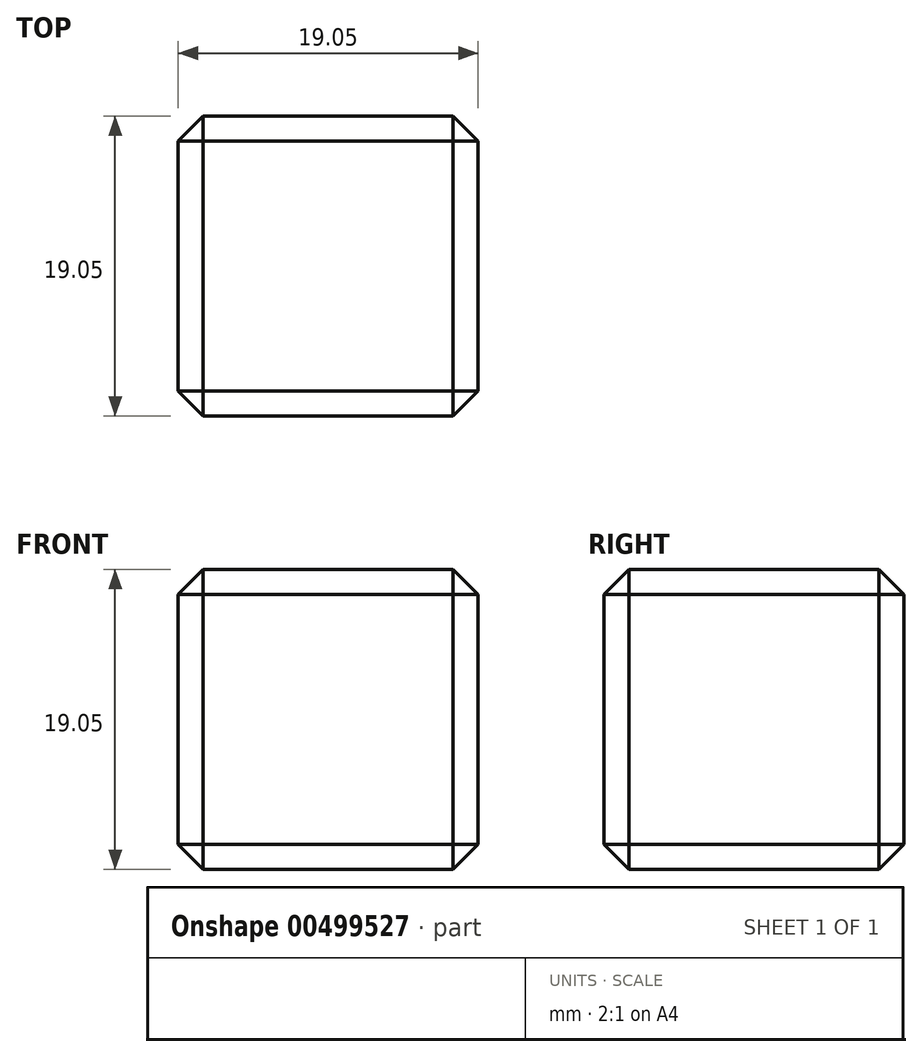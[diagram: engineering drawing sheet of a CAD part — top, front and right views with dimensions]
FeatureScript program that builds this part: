
annotation { "Feature Type Name" : "Feature", "Feature Type Description" : "" }
export const myFeature = defineFeature(function(context is Context, id is Id, definition is map)
    precondition{}
    {
        {
            var Q0;
            Q0=qCreatedBy(makeId("Top.planeOp"),FACE);
            var sketch = newSketch(context, id + "F0", { "sketchPlane" : qUnion([Q0])});
            skLineSegment(sketch, "E0.bottom", {"start": v(0, 0) * mm, "end": v(19.05, 0) * mm});
            skLineSegment(sketch, "E0.top", {"start": v(0, -19.05) * mm, "end": v(19.05, -19.05) * mm});
            skLineSegment(sketch, "E0.left", {"start": v(0, 0) * mm, "end": v(0, -19.05) * mm});
            skLineSegment(sketch, "E0.right", {"start": v(19.05, 0) * mm, "end": v(19.05, -19.05) * mm});
            skSolve(sketch);
        }
        {
            var Q0;
            Q0 = qSketchRegion(id + "F0", true);
            extrude(context, id + "F1", {"entities" : qUnion([Q0]), "depth" : 19.05 * mm});
        }
        {
            var Q0;
            Q0=makeQuery(id+"F1.opExtrude","SWEPT_EDGE",EDGE,{"disambiguationData":[OSD([sQuery(id+"F0.wireOp",EDGE,"E0.top"),sQuery(id+"F0.wireOp",EDGE,"E0.right")])]});
            var Q1;
            Q1=makeQuery(id+"F1.opExtrude","CAP_EDGE",EDGE,{"disambiguationData":[OSD([sQuery(id+"F0.wireOp",EDGE,"E0.top")])],"isStart":true});
            var Q2;
            Q2=makeQuery(id+"F1.opExtrude","CAP_EDGE",EDGE,{"disambiguationData":[OSD([sQuery(id+"F0.wireOp",EDGE,"E0.right")])],"isStart":true});
            var Q3;
            Q3=makeQuery(id+"F1.opExtrude","SWEPT_EDGE",EDGE,{"disambiguationData":[OSD([sQuery(id+"F0.wireOp",EDGE,"E0.bottom"),sQuery(id+"F0.wireOp",EDGE,"E0.right")])]});
            var Q4;
            Q4=makeQuery(id+"F1.opExtrude","CAP_EDGE",EDGE,{"disambiguationData":[OSD([sQuery(id+"F0.wireOp",EDGE,"E0.right")])],"isStart":false});
            var Q5;
            Q5=makeQuery(id+"F1.opExtrude","CAP_EDGE",EDGE,{"disambiguationData":[OSD([sQuery(id+"F0.wireOp",EDGE,"E0.top")])],"isStart":false});
            var Q6;
            Q6=makeQuery(id+"F1.opExtrude","SWEPT_EDGE",EDGE,{"disambiguationData":[OSD([sQuery(id+"F0.wireOp",EDGE,"E0.top"),sQuery(id+"F0.wireOp",EDGE,"E0.left")])]});
            var Q7;
            Q7=makeQuery(id+"F1.opExtrude","CAP_EDGE",EDGE,{"disambiguationData":[OSD([sQuery(id+"F0.wireOp",EDGE,"E0.bottom")])],"isStart":true});
            var Q8;
            Q8=makeQuery(id+"F1.opExtrude","CAP_EDGE",EDGE,{"disambiguationData":[OSD([sQuery(id+"F0.wireOp",EDGE,"E0.left")])],"isStart":true});
            var Q9;
            Q9=makeQuery(id+"F1.opExtrude","CAP_EDGE",EDGE,{"disambiguationData":[OSD([sQuery(id+"F0.wireOp",EDGE,"E0.left")])],"isStart":false});
            var Q10;
            Q10=makeQuery(id+"F1.opExtrude","SWEPT_EDGE",EDGE,{"disambiguationData":[OSD([sQuery(id+"F0.wireOp",EDGE,"E0.bottom"),sQuery(id+"F0.wireOp",EDGE,"E0.left")])]});
            var Q11;
            Q11=makeQuery(id+"F1.opExtrude","CAP_EDGE",EDGE,{"disambiguationData":[OSD([sQuery(id+"F0.wireOp",EDGE,"E0.bottom")])],"isStart":false});
            chamfer(context, id + "F2", {"entities" : qUnion([Q0, Q1, Q2, Q3, Q4, Q5, Q6, Q7, Q8, Q9, Q10, Q11]), "width" : 1.59 * mm, "tangentPropagation" : true});
        }
    });
